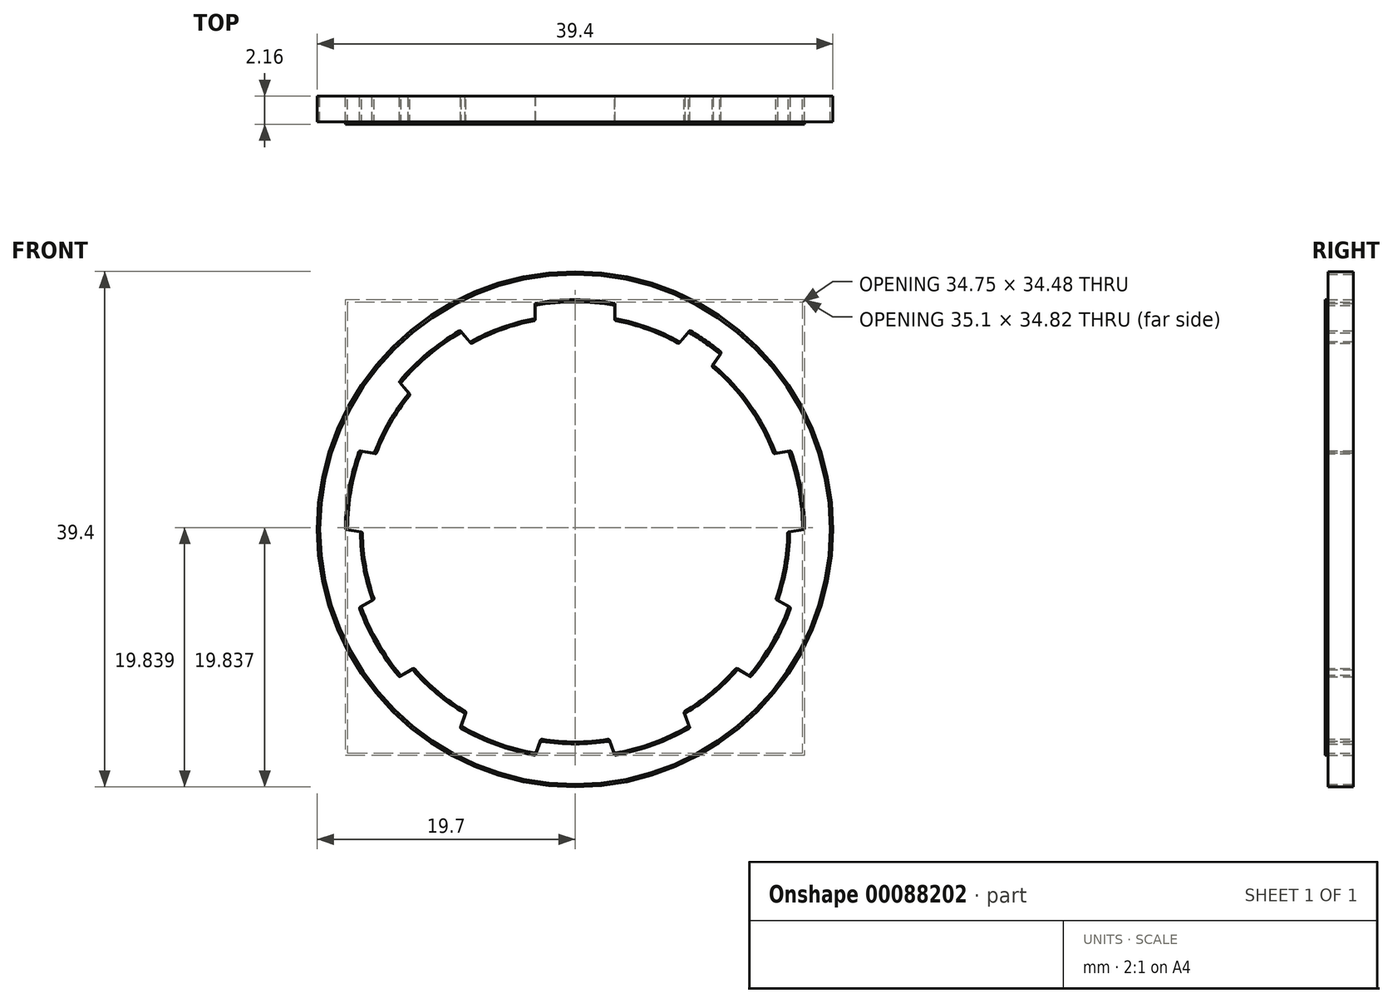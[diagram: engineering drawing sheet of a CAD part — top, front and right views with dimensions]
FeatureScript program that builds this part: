
annotation { "Feature Type Name" : "Feature", "Feature Type Description" : "" }
export const myFeature = defineFeature(function(context is Context, id is Id, definition is map)
    precondition{}
    {
        {
            var Q0;
            Q0=qCreatedBy(makeId("Front.planeOp"),FACE);
            var sketch = newSketch(context, id + "F5", { "sketchPlane" : qUnion([Q0])});
            skCircle(sketch, "E0", {"center": v(0, 0) * mm, "radius": 17.38 * mm});
            skCircle(sketch, "E1", {"center": v(0, 0) * mm, "radius": 16.25 * mm});
            skLineSegment(sketch, "E2", {"start": v(-3.03, 15.96) * mm, "end": v(-3.03, 17.1) * mm});
            skLineSegment(sketch, "E3", {"start": v(-3.03, 17.1) * mm, "end": v(3.03, 17.1) * mm, "construction": true});
            skLineSegment(sketch, "E4", {"start": v(3.03, 17.1) * mm, "end": v(3.03, 15.96) * mm});
            skLineSegment(sketch, "E5", {"start": v(0, 0) * mm, "end": v(0, 17.1) * mm, "construction": true});
            skLineSegment(sketch, "E6", {"start": v(0, 17.1) * mm, "end": v(0, 17.1) * mm});
            skLineSegment(sketch, "E7", {"start": v(0, 0) * mm, "end": v(-3.03, 15.96) * mm, "construction": true});
            skLineSegment(sketch, "E8", {"start": v(0, 0) * mm, "end": v(3.03, 15.96) * mm, "construction": true});
            skLineSegment(sketch, "E9", {"start": v(0, 0) * mm, "end": v(-7.94, 14.18) * mm, "construction": true});
            skLineSegment(sketch, "E10", {"start": v(0, 0) * mm, "end": v(-12.58, 10.28) * mm, "construction": true});
            skLineSegment(sketch, "E11", {"start": v(-12.58, 10.28) * mm, "end": v(-13.32, 11.16) * mm});
            skLineSegment(sketch, "E12", {"start": v(-7.94, 14.18) * mm, "end": v(-8.68, 15.05) * mm});
            skLineSegment(sketch, "E13", {"start": v(-13.32, 11.16) * mm, "end": v(-8.68, 15.05) * mm, "construction": true});
            skLineSegment(sketch, "E14", {"start": v(0, 0) * mm, "end": v(-11, 13.1) * mm, "construction": true});
            skCircle(sketch, "E15", {"center": v(0, 0) * mm, "radius": 19.5 * mm});
            skLineSegment(sketch, "E16", {"start": v(0, 0) * mm, "end": v(9.83, 14.24) * mm, "construction": true});
            skLineSegment(sketch, "E17", {"start": v(7.94, 14.18) * mm, "end": v(8.58, 15.1) * mm});
            skLineSegment(sketch, "E18", {"start": v(8.58, 15.1) * mm, "end": v(11.09, 13.38) * mm, "construction": true});
            skLineSegment(sketch, "E19", {"start": v(11.09, 13.38) * mm, "end": v(10.45, 12.45) * mm});
            skLineSegment(sketch, "E20", {"start": v(0, 0) * mm, "end": v(7.94, 14.18) * mm, "construction": true});
            skLineSegment(sketch, "E21", {"start": v(0, 0) * mm, "end": v(10.45, 12.45) * mm, "construction": true});
            skLineSegment(sketch, "E22", {"start": v(0, 0) * mm, "end": v(16.85, 2.97) * mm, "construction": true});
            skLineSegment(sketch, "E23", {"start": v(15.2, 5.76) * mm, "end": v(16.32, 5.96) * mm});
            skLineSegment(sketch, "E24", {"start": v(16.32, 5.96) * mm, "end": v(17.37, -0.01) * mm, "construction": true});
            skLineSegment(sketch, "E25", {"start": v(17.37, -0.01) * mm, "end": v(16.25, -0.21) * mm});
            skLineSegment(sketch, "E26", {"start": v(0, 0) * mm, "end": v(15.2, 5.76) * mm, "construction": true});
            skLineSegment(sketch, "E27", {"start": v(0, 0) * mm, "end": v(16.25, -0.21) * mm, "construction": true});
            skSolve(sketch);
        }
        {
            var Q0;
            {var subQ0=sQuery(id+"F5.wireOp",EDGE,"E2");Q0=makeQuery(id+"F5.imprint","IMPRINT",FACE,{"disambiguationData":[TD([[makeQuery(id+"F5.imprint","IMPRINT",EDGE,{"derivedFrom":subQ0}),1.0]])]});}
            extrude(context, id + "F0", {"entities" : qUnion([Q0]), "endBound" : BoundingType.SYMMETRIC, "depth" : 2.15 * mm});
        }
        {
            var Q0;
            Q0=qCreatedBy(makeId("Top.planeOp"),FACE);
            var sketch = newSketch(context, id + "F6", { "sketchPlane" : qUnion([Q0])});
            skLineSegment(sketch, "E28", {"start": v(0, 0) * mm, "end": v(0, -24.77) * mm, "construction": true});
            skSolve(sketch);
        }
        {
            var Q0;
            Q0=makeQuery(id+"F0.opExtrude","SWEPT_BODY",BODY,{"disambiguationData":[OSD([sQuery(id+"F5.wireOp",EDGE,"E0"),sQuery(id+"F5.wireOp",EDGE,"E1"),sQuery(id+"F5.wireOp",EDGE,"E2"),sQuery(id+"F5.wireOp",EDGE,"E12")])]});
            var Q1;
            Q1=sQuery(id+"F6.wireOp",EDGE,"E28");
            circularPattern(context, id + "F7", {"entities" : qUnion([Q0]), "axis" : qUnion([Q1]), "angle" : 360 * degree, "instanceCount" : 9, "equalSpace" : true});
        }
        {
            var Q0;
            {var subQ0=sQuery(id+"F5.wireOp",EDGE,"E4");Q0=makeQuery(id+"F5.imprint","IMPRINT",FACE,{"disambiguationData":[TD([[makeQuery(id+"F5.imprint","IMPRINT",EDGE,{"derivedFrom":subQ0}),1.0]])]});}
            var Q1;
            {var subQ0=sQuery(id+"F5.wireOp",EDGE,"E19");Q1=makeQuery(id+"F5.imprint","IMPRINT",FACE,{"disambiguationData":[TD([[makeQuery(id+"F5.imprint","IMPRINT",EDGE,{"derivedFrom":subQ0}),1.0]])]});}
            extrude(context, id + "F8", {"entities" : qUnion([Q0, Q1]), "operationType" : NewBodyOperationType.ADD, "endBound" : BoundingType.SYMMETRIC, "depth" : 2.15 * mm});
        }
        {
            var Q0;
            Q0=makeQuery(id+"F5.imprint","IMPRINT",FACE,{"disambiguationData":[TD([[makeQuery(id+"F5.imprint","IMPRINT",EDGE,{"derivedFrom":sQuery(id+"F5.wireOp",EDGE,"E15")}),1.0]])]});
            extrude(context, id + "F1", {"entities" : qUnion([Q0]), "operationType" : NewBodyOperationType.ADD, "endBound" : BoundingType.SYMMETRIC, "depth" : 2.15 * mm});
        }
        {
            var Q0;
            Q0=makeQuery(id+"F0.opExtrude","SWEPT_EDGE",EDGE,{"disambiguationData":[OSD([sQuery(id+"F5.wireOp",EDGE,"E1"),sQuery(id+"F5.wireOp",EDGE,"E2")])]});
            var Q1;
            Q1=makeQuery(id+"F7.opPattern","COPY",EDGE,{"derivedFrom":makeQuery(id+"F0.opExtrude","SWEPT_EDGE",EDGE,{"disambiguationData":[OSD([sQuery(id+"F5.wireOp",EDGE,"E1"),sQuery(id+"F5.wireOp",EDGE,"E12")])]}),"instanceName":"8"});
            var Q2;
            Q2=makeQuery(id+"F0.opExtrude","SWEPT_EDGE",EDGE,{"disambiguationData":[OSD([sQuery(id+"F5.wireOp",EDGE,"E0"),sQuery(id+"F5.wireOp",EDGE,"E2")])]});
            var Q3;
            Q3=makeQuery(id+"F7.opPattern","COPY",EDGE,{"derivedFrom":makeQuery(id+"F0.opExtrude","SWEPT_EDGE",EDGE,{"disambiguationData":[OSD([sQuery(id+"F5.wireOp",EDGE,"E1"),sQuery(id+"F5.wireOp",EDGE,"E2")])]}),"instanceName":"8"});
            var Q4;
            Q4=makeQuery(id+"F0.opExtrude","SWEPT_EDGE",EDGE,{"disambiguationData":[OSD([sQuery(id+"F5.wireOp",EDGE,"E1"),sQuery(id+"F5.wireOp",EDGE,"E12")])]});
            var Q5;
            Q5=makeQuery(id+"F7.opPattern","COPY",EDGE,{"derivedFrom":makeQuery(id+"F0.opExtrude","SWEPT_EDGE",EDGE,{"disambiguationData":[OSD([sQuery(id+"F5.wireOp",EDGE,"E0"),sQuery(id+"F5.wireOp",EDGE,"E12")])]}),"instanceName":"8"});
            var Q6;
            Q6=makeQuery(id+"F7.opPattern","COPY",EDGE,{"derivedFrom":makeQuery(id+"F0.opExtrude","SWEPT_EDGE",EDGE,{"disambiguationData":[OSD([sQuery(id+"F5.wireOp",EDGE,"E0"),sQuery(id+"F5.wireOp",EDGE,"E2")])]}),"instanceName":"8"});
            var Q7;
            Q7=makeQuery(id+"F8.opExtrude","SWEPT_EDGE",EDGE,{"disambiguationData":[OSD([sQuery(id+"F5.wireOp",EDGE,"E1"),sQuery(id+"F5.wireOp",EDGE,"E19")])]});
            var Q8;
            Q8=makeQuery(id+"F8.opExtrude","SWEPT_EDGE",EDGE,{"disambiguationData":[OSD([sQuery(id+"F5.wireOp",EDGE,"E0"),sQuery(id+"F5.wireOp",EDGE,"E19")])]});
            var Q9;
            Q9=makeQuery(id+"F7.opPattern","COPY",EDGE,{"derivedFrom":makeQuery(id+"F0.opExtrude","SWEPT_EDGE",EDGE,{"disambiguationData":[OSD([sQuery(id+"F5.wireOp",EDGE,"E1"),sQuery(id+"F5.wireOp",EDGE,"E2")])]}),"instanceName":"7"});
            var Q10;
            Q10=makeQuery(id+"F7.opPattern","COPY",EDGE,{"derivedFrom":makeQuery(id+"F0.opExtrude","SWEPT_EDGE",EDGE,{"disambiguationData":[OSD([sQuery(id+"F5.wireOp",EDGE,"E0"),sQuery(id+"F5.wireOp",EDGE,"E2")])]}),"instanceName":"7"});
            var Q11;
            Q11=makeQuery(id+"F7.opPattern","COPY",EDGE,{"derivedFrom":makeQuery(id+"F0.opExtrude","SWEPT_EDGE",EDGE,{"disambiguationData":[OSD([sQuery(id+"F5.wireOp",EDGE,"E0"),sQuery(id+"F5.wireOp",EDGE,"E12")])]}),"instanceName":"6"});
            var Q12;
            Q12=makeQuery(id+"F7.opPattern","COPY",EDGE,{"derivedFrom":makeQuery(id+"F0.opExtrude","SWEPT_EDGE",EDGE,{"disambiguationData":[OSD([sQuery(id+"F5.wireOp",EDGE,"E1"),sQuery(id+"F5.wireOp",EDGE,"E12")])]}),"instanceName":"6"});
            var Q13;
            Q13=makeQuery(id+"F7.opPattern","COPY",EDGE,{"derivedFrom":makeQuery(id+"F0.opExtrude","SWEPT_EDGE",EDGE,{"disambiguationData":[OSD([sQuery(id+"F5.wireOp",EDGE,"E1"),sQuery(id+"F5.wireOp",EDGE,"E2")])]}),"instanceName":"6"});
            var Q14;
            Q14=makeQuery(id+"F7.opPattern","COPY",EDGE,{"derivedFrom":makeQuery(id+"F0.opExtrude","SWEPT_EDGE",EDGE,{"disambiguationData":[OSD([sQuery(id+"F5.wireOp",EDGE,"E0"),sQuery(id+"F5.wireOp",EDGE,"E2")])]}),"instanceName":"6"});
            var Q15;
            Q15=makeQuery(id+"F7.opPattern","COPY",EDGE,{"derivedFrom":makeQuery(id+"F0.opExtrude","SWEPT_EDGE",EDGE,{"disambiguationData":[OSD([sQuery(id+"F5.wireOp",EDGE,"E1"),sQuery(id+"F5.wireOp",EDGE,"E12")])]}),"instanceName":"5"});
            var Q16;
            Q16=makeQuery(id+"F7.opPattern","COPY",EDGE,{"derivedFrom":makeQuery(id+"F0.opExtrude","SWEPT_EDGE",EDGE,{"disambiguationData":[OSD([sQuery(id+"F5.wireOp",EDGE,"E1"),sQuery(id+"F5.wireOp",EDGE,"E2")])]}),"instanceName":"5"});
            var Q17;
            Q17=makeQuery(id+"F7.opPattern","COPY",EDGE,{"derivedFrom":makeQuery(id+"F0.opExtrude","SWEPT_EDGE",EDGE,{"disambiguationData":[OSD([sQuery(id+"F5.wireOp",EDGE,"E0"),sQuery(id+"F5.wireOp",EDGE,"E2")])]}),"instanceName":"5"});
            var Q18;
            Q18=makeQuery(id+"F7.opPattern","COPY",EDGE,{"derivedFrom":makeQuery(id+"F0.opExtrude","SWEPT_EDGE",EDGE,{"disambiguationData":[OSD([sQuery(id+"F5.wireOp",EDGE,"E0"),sQuery(id+"F5.wireOp",EDGE,"E12")])]}),"instanceName":"5"});
            var Q19;
            Q19=makeQuery(id+"F7.opPattern","COPY",EDGE,{"derivedFrom":makeQuery(id+"F0.opExtrude","SWEPT_EDGE",EDGE,{"disambiguationData":[OSD([sQuery(id+"F5.wireOp",EDGE,"E0"),sQuery(id+"F5.wireOp",EDGE,"E12")])]}),"instanceName":"4"});
            var Q20;
            Q20=makeQuery(id+"F7.opPattern","COPY",EDGE,{"derivedFrom":makeQuery(id+"F0.opExtrude","SWEPT_EDGE",EDGE,{"disambiguationData":[OSD([sQuery(id+"F5.wireOp",EDGE,"E1"),sQuery(id+"F5.wireOp",EDGE,"E12")])]}),"instanceName":"4"});
            var Q21;
            Q21=makeQuery(id+"F7.opPattern","COPY",EDGE,{"derivedFrom":makeQuery(id+"F0.opExtrude","SWEPT_EDGE",EDGE,{"disambiguationData":[OSD([sQuery(id+"F5.wireOp",EDGE,"E1"),sQuery(id+"F5.wireOp",EDGE,"E2")])]}),"instanceName":"4"});
            var Q22;
            Q22=makeQuery(id+"F7.opPattern","COPY",EDGE,{"derivedFrom":makeQuery(id+"F0.opExtrude","SWEPT_EDGE",EDGE,{"disambiguationData":[OSD([sQuery(id+"F5.wireOp",EDGE,"E0"),sQuery(id+"F5.wireOp",EDGE,"E2")])]}),"instanceName":"4"});
            var Q23;
            Q23=makeQuery(id+"F7.opPattern","COPY",EDGE,{"derivedFrom":makeQuery(id+"F0.opExtrude","SWEPT_EDGE",EDGE,{"disambiguationData":[OSD([sQuery(id+"F5.wireOp",EDGE,"E1"),sQuery(id+"F5.wireOp",EDGE,"E12")])]}),"instanceName":"3"});
            var Q24;
            Q24=makeQuery(id+"F7.opPattern","COPY",EDGE,{"derivedFrom":makeQuery(id+"F0.opExtrude","SWEPT_EDGE",EDGE,{"disambiguationData":[OSD([sQuery(id+"F5.wireOp",EDGE,"E0"),sQuery(id+"F5.wireOp",EDGE,"E12")])]}),"instanceName":"3"});
            var Q25;
            Q25=makeQuery(id+"F7.opPattern","COPY",EDGE,{"derivedFrom":makeQuery(id+"F0.opExtrude","SWEPT_EDGE",EDGE,{"disambiguationData":[OSD([sQuery(id+"F5.wireOp",EDGE,"E1"),sQuery(id+"F5.wireOp",EDGE,"E2")])]}),"instanceName":"3"});
            var Q26;
            Q26=makeQuery(id+"F7.opPattern","COPY",EDGE,{"derivedFrom":makeQuery(id+"F0.opExtrude","SWEPT_EDGE",EDGE,{"disambiguationData":[OSD([sQuery(id+"F5.wireOp",EDGE,"E0"),sQuery(id+"F5.wireOp",EDGE,"E2")])]}),"instanceName":"3"});
            var Q27;
            Q27=makeQuery(id+"F7.opPattern","COPY",EDGE,{"derivedFrom":makeQuery(id+"F0.opExtrude","SWEPT_EDGE",EDGE,{"disambiguationData":[OSD([sQuery(id+"F5.wireOp",EDGE,"E1"),sQuery(id+"F5.wireOp",EDGE,"E12")])]}),"instanceName":"2"});
            var Q28;
            Q28=makeQuery(id+"F7.opPattern","COPY",EDGE,{"derivedFrom":makeQuery(id+"F0.opExtrude","SWEPT_EDGE",EDGE,{"disambiguationData":[OSD([sQuery(id+"F5.wireOp",EDGE,"E0"),sQuery(id+"F5.wireOp",EDGE,"E12")])]}),"instanceName":"2"});
            var Q29;
            Q29=makeQuery(id+"F7.opPattern","COPY",EDGE,{"derivedFrom":makeQuery(id+"F0.opExtrude","SWEPT_EDGE",EDGE,{"disambiguationData":[OSD([sQuery(id+"F5.wireOp",EDGE,"E1"),sQuery(id+"F5.wireOp",EDGE,"E2")])]}),"instanceName":"2"});
            var Q30;
            Q30=makeQuery(id+"F7.opPattern","COPY",EDGE,{"derivedFrom":makeQuery(id+"F0.opExtrude","SWEPT_EDGE",EDGE,{"disambiguationData":[OSD([sQuery(id+"F5.wireOp",EDGE,"E0"),sQuery(id+"F5.wireOp",EDGE,"E2")])]}),"instanceName":"2"});
            var Q31;
            Q31=makeQuery(id+"F7.opPattern","COPY",EDGE,{"derivedFrom":makeQuery(id+"F0.opExtrude","SWEPT_EDGE",EDGE,{"disambiguationData":[OSD([sQuery(id+"F5.wireOp",EDGE,"E1"),sQuery(id+"F5.wireOp",EDGE,"E12")])]}),"instanceName":"1"});
            var Q32;
            Q32=makeQuery(id+"F7.opPattern","COPY",EDGE,{"derivedFrom":makeQuery(id+"F0.opExtrude","SWEPT_EDGE",EDGE,{"disambiguationData":[OSD([sQuery(id+"F5.wireOp",EDGE,"E0"),sQuery(id+"F5.wireOp",EDGE,"E12")])]}),"instanceName":"1"});
            var Q33;
            Q33=makeQuery(id+"F7.opPattern","COPY",EDGE,{"derivedFrom":makeQuery(id+"F0.opExtrude","SWEPT_EDGE",EDGE,{"disambiguationData":[OSD([sQuery(id+"F5.wireOp",EDGE,"E0"),sQuery(id+"F5.wireOp",EDGE,"E2")])]}),"instanceName":"1"});
            var Q34;
            Q34=makeQuery(id+"F7.opPattern","COPY",EDGE,{"derivedFrom":makeQuery(id+"F0.opExtrude","SWEPT_EDGE",EDGE,{"disambiguationData":[OSD([sQuery(id+"F5.wireOp",EDGE,"E1"),sQuery(id+"F5.wireOp",EDGE,"E2")])]}),"instanceName":"1"});
            var Q35;
            Q35=makeQuery(id+"F0.opExtrude","SWEPT_EDGE",EDGE,{"disambiguationData":[OSD([sQuery(id+"F5.wireOp",EDGE,"E0"),sQuery(id+"F5.wireOp",EDGE,"E12")])]});
            fillet(context, id + "F2", {"entities" : qUnion([Q0, Q1, Q2, Q3, Q4, Q5, Q6, Q7, Q8, Q9, Q10, Q11, Q12, Q13, Q14, Q15, Q16, Q17, Q18, Q19, Q20, Q21, Q22, Q23, Q24, Q25, Q26, Q27, Q28, Q29, Q30, Q31, Q32, Q33, Q34, Q35]), "radius" : 0.1 * mm, "tangentPropagation" : true, "allowEdgeOverflow" : false});
        }
        {
            var Q0;
            Q0=makeQuery(id+"F0.opExtrude","SWEPT_BODY",BODY,{"disambiguationData":[OSD([sQuery(id+"F5.wireOp",EDGE,"E0"),sQuery(id+"F5.wireOp",EDGE,"E1"),sQuery(id+"F5.wireOp",EDGE,"E2"),sQuery(id+"F5.wireOp",EDGE,"E12")])]});
            var Q1;
            Q1=qCreatedBy(makeId("Origin.pointOp"),VERTEX);
            transform(context, id + "F3", {"entities" : qUnion([Q0]), "transformType" : TransformType.SCALE_UNIFORMLY, "scale" : 1.01, "scalePoint" : qUnion([Q1]), "makeCopy" : true});
        }
        {
            var Q0;
            {var subQ0=sQuery(id+"F5.wireOp",EDGE,"E0");var subQ1=sQuery(id+"F5.wireOp",EDGE,"E1");var subQ2=makeQuery(id+"F0.opExtrude","CAP_FACE",FACE,{"disambiguationData":[OSD([subQ0,subQ1,sQuery(id+"F5.wireOp",EDGE,"E2"),sQuery(id+"F5.wireOp",EDGE,"E12")])],"isStart":false});Q0=makeQuery(id+"F3.opPattern","COPY",FACE,{"derivedFrom":makeQuery(id+"F1.boolean.opBoolean","MERGE",FACE,{"derivedFrom":[subQ2,makeQuery(id+"F7.opPattern","COPY",FACE,{"derivedFrom":subQ2,"instanceName":"1"}),makeQuery(id+"F7.opPattern","COPY",FACE,{"derivedFrom":subQ2,"instanceName":"2"}),makeQuery(id+"F7.opPattern","COPY",FACE,{"derivedFrom":subQ2,"instanceName":"3"}),makeQuery(id+"F7.opPattern","COPY",FACE,{"derivedFrom":subQ2,"instanceName":"4"}),makeQuery(id+"F7.opPattern","COPY",FACE,{"derivedFrom":subQ2,"instanceName":"5"}),makeQuery(id+"F7.opPattern","COPY",FACE,{"derivedFrom":subQ2,"instanceName":"6"}),makeQuery(id+"F8.boolean.opBoolean","MERGE",FACE,{"derivedFrom":[makeQuery(id+"F7.opPattern","COPY",FACE,{"derivedFrom":subQ2,"instanceName":"7"}),makeQuery(id+"F8.opExtrude","CAP_FACE",FACE,{"disambiguationData":[OSD([subQ0,subQ1,sQuery(id+"F5.wireOp",EDGE,"E19"),sQuery(id+"F5.wireOp",EDGE,"E23")])],"isStart":false})]}),makeQuery(id+"F7.opPattern","COPY",FACE,{"derivedFrom":subQ2,"instanceName":"8"}),makeQuery(id+"F1.opExtrude","CAP_FACE",FACE,{"disambiguationData":[OSD([subQ0,sQuery(id+"F5.wireOp",EDGE,"E15")])],"isStart":false})]}),"instanceName":"1"});}
            extrude(context, id + "F4", {"entities" : qUnion([Q0]), "operationType" : NewBodyOperationType.REMOVE, "oppositeDirection" : true, "depth" : .215 * mm});
        }
    });
